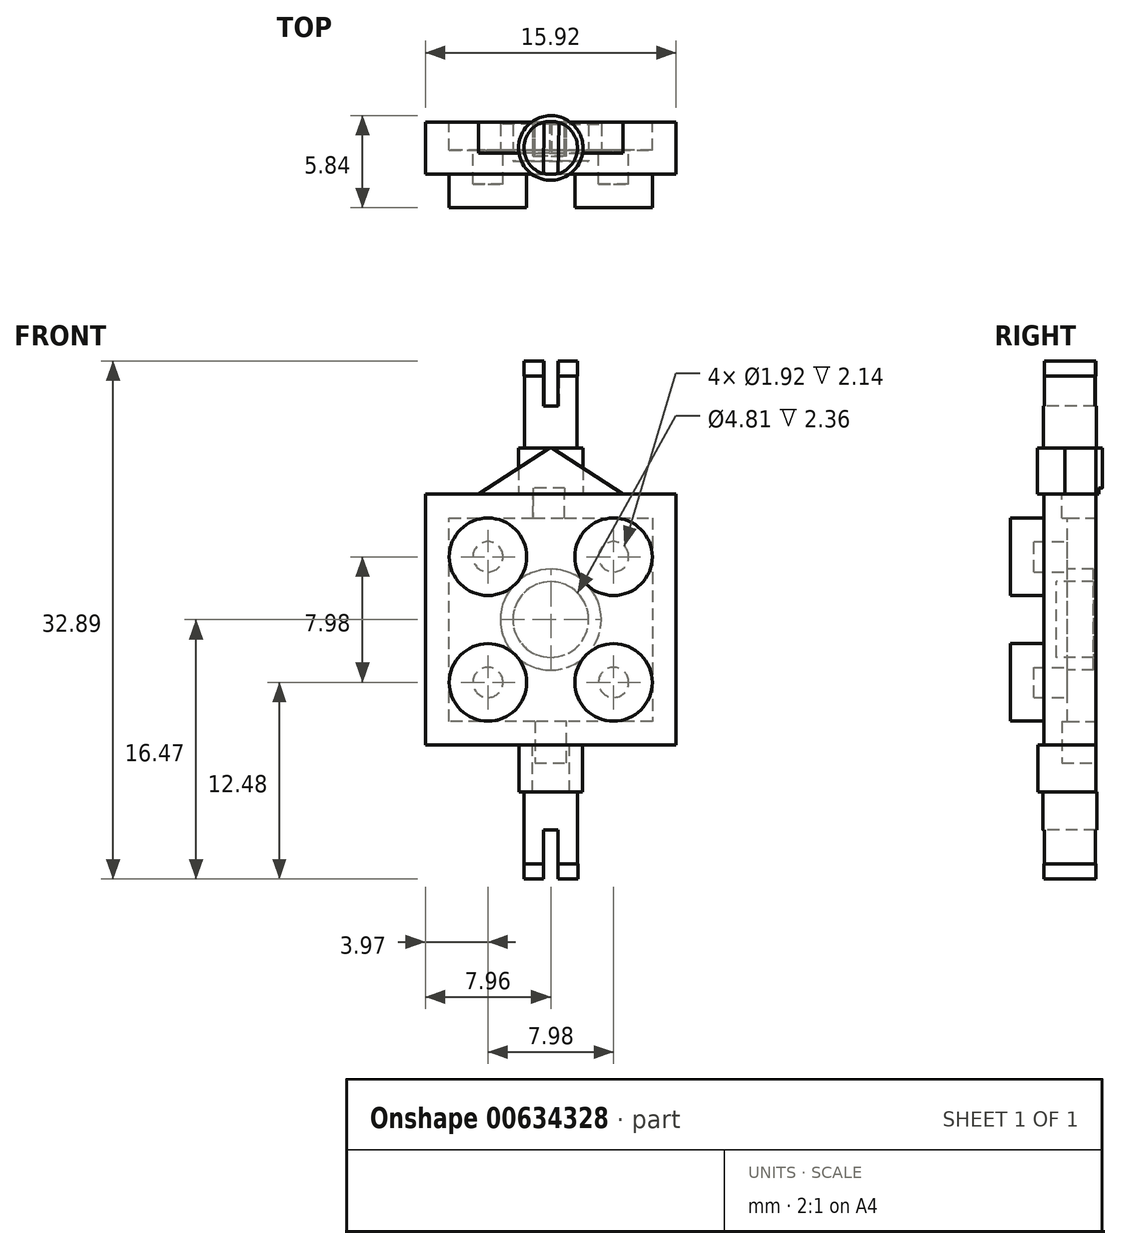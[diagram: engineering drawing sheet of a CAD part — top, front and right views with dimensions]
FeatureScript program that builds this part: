
annotation { "Feature Type Name" : "Feature", "Feature Type Description" : "" }
export const myFeature = defineFeature(function(context is Context, id is Id, definition is map)
    precondition{}
    {
        {
            var Q0;
            Q0=qCreatedBy(makeId("Front.planeOp"),FACE);
            var sketch = newSketch(context, id + "F0", { "sketchPlane" : qUnion([Q0])});
            skLineSegment(sketch, "E0", {"start": v(0, 0) * mm, "end": v(0, 15.92) * mm});
            skLineSegment(sketch, "E1", {"start": v(0, 15.92) * mm, "end": v(15.92, 15.92) * mm});
            skLineSegment(sketch, "E2", {"start": v(15.92, 15.92) * mm, "end": v(15.92, 0) * mm});
            skLineSegment(sketch, "E3", {"start": v(15.92, 0) * mm, "end": v(0, 0) * mm});
            skSolve(sketch);
        }
        {
            var Q0;
            Q0=makeQuery(id+"F0.imprint","IMPRINT",FACE,{"disambiguationData":[TD([[makeQuery(id+"F0.imprint","IMPRINT",EDGE,{"derivedFrom":sQuery(id+"F0.wireOp",EDGE,"E0")}),-1.0]])]});
            extrude(context, id + "F1", {"entities" : qUnion([Q0]), "depth" : 3.3 * mm});
        }
        {
            var Q0;
            Q0=makeQuery(id+"F1.opExtrude","CAP_FACE",FACE,{"disambiguationData":[OSD([sQuery(id+"F0.wireOp",EDGE,"E0"),sQuery(id+"F0.wireOp",EDGE,"E1"),sQuery(id+"F0.wireOp",EDGE,"E2"),sQuery(id+"F0.wireOp",EDGE,"E3")])],"isStart":false});
            var sketch = newSketch(context, id + "F2", { "sketchPlane" : qUnion([Q0])});
            skCircle(sketch, "E4", {"center": v(3.97, 11.95) * mm, "radius": 2.46 * mm});
            skCircle(sketch, "E5", {"center": v(11.95, 11.95) * mm, "radius": 2.46 * mm});
            skCircle(sketch, "E6", {"center": v(3.97, 3.97) * mm, "radius": 2.46 * mm});
            skCircle(sketch, "E7", {"center": v(11.95, 3.97) * mm, "radius": 2.46 * mm});
            skSolve(sketch);
        }
        {
            var Q0;
            Q0=qSketchRegion(id+"F2",true);
            extrude(context, id + "F3", {"entities" : qUnion([Q0]), "operationType" : NewBodyOperationType.ADD, "depth" : 2.14 * mm});
        }
        {
            var Q0;
            Q0=makeQuery(id+"F1.opExtrude","CAP_FACE",FACE,{"disambiguationData":[OSD([sQuery(id+"F0.wireOp",EDGE,"E0"),sQuery(id+"F0.wireOp",EDGE,"E1"),sQuery(id+"F0.wireOp",EDGE,"E2"),sQuery(id+"F0.wireOp",EDGE,"E3")])],"isStart":true});
            shell(context, id + "F4", {"entities" : qUnion([Q0]), "thickness" : 1.5 * mm});
        }
        {
            var Q0;
            Q0=makeQuery(id+"F4.opShell","OFFSET_FACE",FACE,{"disambiguationData":[OSD([sQuery(id+"F0.wireOp",EDGE,"E0"),sQuery(id+"F0.wireOp",EDGE,"E1"),sQuery(id+"F0.wireOp",EDGE,"E2"),sQuery(id+"F0.wireOp",EDGE,"E3")])]});
            var sketch = newSketch(context, id + "F5", { "sketchPlane" : qUnion([Q0])});
            skCircle(sketch, "E8", {"center": v(-7.96, 7.96) * mm, "radius": 3.2 * mm});
            skPoint(sketch, "E8.centerSnap0", {"position": v(-7.96, 14.42) * mm});
            skPoint(sketch, "E8.centerSnap1", {"position": v(-1.5, 7.96) * mm});
            skSolve(sketch);
        }
        {
            var Q0;
            Q0=makeQuery(id+"F5.imprint","IMPRINT",FACE,{"disambiguationData":[TD([[makeQuery(id+"F5.imprint","IMPRINT",EDGE,{"derivedFrom":sQuery(id+"F5.wireOp",EDGE,"E8")}),1.0]])]});
            extrude(context, id + "F6", {"entities" : qUnion([Q0]), "operationType" : NewBodyOperationType.ADD, "depth" : 1.66 * mm});
        }
        {
            var Q0;
            Q0=makeQuery(id+"F6.opExtrude","CAP_FACE",FACE,{"disambiguationData":[OSD([sQuery(id+"F5.wireOp",EDGE,"E8")])],"isStart":false});
            shell(context, id + "F7", {"entities" : qUnion([Q0]), "thickness" : .80 * mm});
        }
        {
            var Q0;
            Q0=makeQuery(id+"F1.opExtrude","SWEPT_FACE",FACE,{"disambiguationData":[OSD([sQuery(id+"F0.wireOp",EDGE,"E3")])]});
            var sketch = newSketch(context, id + "F8", { "sketchPlane" : qUnion([Q0])});
            skCircle(sketch, "E9", {"center": v(7.96, 1.65) * mm, "radius": 2.02 * mm});
            skPoint(sketch, "E9.centerSnap0", {"position": v(7.96, 3.3) * mm});
            skPoint(sketch, "E9.centerSnap1", {"position": v(0, 1.65) * mm});
            skSolve(sketch);
        }
        {
            var Q0;
            {var subQ0=sQuery(id+"F8.wireOp",EDGE,"E9");var subQ1=makeQuery(id+"F1.opExtrude","CAP_EDGE",EDGE,{"disambiguationData":[OSD([sQuery(id+"F0.wireOp",EDGE,"E3")])],"isStart":false});var subQ2=makeQuery(id+"F8.imprint","INTERSECT",VERTEX,{"disambiguationData":[OD(0.0)],"derivedFrom":[subQ1,subQ0]});Q0=makeQuery(id+"F8.imprint","IMPRINT",FACE,{"disambiguationData":[TD([[makeQuery(id+"F8.imprint","IMPRINT",EDGE,{"disambiguationData":[TD([[subQ2,1.0]])],"derivedFrom":subQ0}),1.0]])]});}
            var Q1;
            {var subQ0=sQuery(id+"F8.wireOp",EDGE,"E9");var subQ1=makeQuery(id+"F1.opExtrude","CAP_EDGE",EDGE,{"disambiguationData":[OSD([sQuery(id+"F0.wireOp",EDGE,"E3")])],"isStart":true});var subQ2=makeQuery(id+"F8.imprint","INTERSECT",VERTEX,{"disambiguationData":[OD(0.0)],"derivedFrom":[subQ1,subQ0]});Q1=makeQuery(id+"F8.imprint","IMPRINT",FACE,{"disambiguationData":[TD([[makeQuery(id+"F8.imprint","IMPRINT",EDGE,{"disambiguationData":[TD([[subQ2,-1.0]])],"derivedFrom":subQ0}),1.0]])]});}
            var Q2;
            {var subQ0=sQuery(id+"F8.wireOp",EDGE,"E9");var subQ1=sQuery(id+"F0.wireOp",EDGE,"E3");var subQ2=makeQuery(id+"F1.opExtrude","CAP_EDGE",EDGE,{"disambiguationData":[OSD([subQ1])],"isStart":false});var subQ3=makeQuery(id+"F8.imprint","INTERSECT",VERTEX,{"disambiguationData":[OD(0.0)],"derivedFrom":[subQ2,subQ0]});Q2=makeQuery(id+"F8.imprint","IMPRINT",FACE,{"disambiguationData":[TD([[makeQuery(id+"F8.imprint","IMPRINT",EDGE,{"disambiguationData":[TD([[subQ3,-1.0]])],"derivedFrom":subQ0}),1.0]])]});}
            extrude(context, id + "F9", {"entities" : qUnion([Q0, Q1, Q2]), "operationType" : NewBodyOperationType.ADD, "depth" : 8 * mm});
        }
        {
            var Q0;
            Q0=makeQuery(id+"F1.opExtrude","SWEPT_FACE",FACE,{"disambiguationData":[OSD([sQuery(id+"F0.wireOp",EDGE,"E1")])]});
            var sketch = newSketch(context, id + "F10", { "sketchPlane" : qUnion([Q0])});
            skCircle(sketch, "E10", {"center": v(7.96, -1.65) * mm, "radius": 2.05 * mm});
            skPoint(sketch, "E10.centerSnap0", {"position": v(7.96, -3.3) * mm});
            skPoint(sketch, "E10.centerSnap1", {"position": v(15.92, -1.65) * mm});
            skSolve(sketch);
        }
        {
            var Q0;
            {var subQ0=sQuery(id+"F10.wireOp",EDGE,"E10");var subQ1=makeQuery(id+"F1.opExtrude","CAP_EDGE",EDGE,{"disambiguationData":[OSD([sQuery(id+"F0.wireOp",EDGE,"E1")])],"isStart":true});var subQ2=makeQuery(id+"F10.imprint","INTERSECT",VERTEX,{"disambiguationData":[OD(0.0)],"derivedFrom":[subQ1,subQ0]});Q0=makeQuery(id+"F10.imprint","IMPRINT",FACE,{"disambiguationData":[TD([[makeQuery(id+"F10.imprint","IMPRINT",EDGE,{"disambiguationData":[TD([[subQ2,1.0]])],"derivedFrom":subQ0}),1.0]])]});}
            var Q1;
            {var subQ0=sQuery(id+"F10.wireOp",EDGE,"E10");var subQ1=makeQuery(id+"F1.opExtrude","CAP_EDGE",EDGE,{"disambiguationData":[OSD([sQuery(id+"F0.wireOp",EDGE,"E1")])],"isStart":false});var subQ2=makeQuery(id+"F10.imprint","INTERSECT",VERTEX,{"disambiguationData":[OD(0.0)],"derivedFrom":[subQ1,subQ0]});Q1=makeQuery(id+"F10.imprint","IMPRINT",FACE,{"disambiguationData":[TD([[makeQuery(id+"F10.imprint","IMPRINT",EDGE,{"disambiguationData":[TD([[subQ2,-1.0]])],"derivedFrom":subQ0}),1.0]])]});}
            var Q2;
            {var subQ0=sQuery(id+"F10.wireOp",EDGE,"E10");var subQ1=sQuery(id+"F0.wireOp",EDGE,"E1");var subQ2=makeQuery(id+"F1.opExtrude","CAP_EDGE",EDGE,{"disambiguationData":[OSD([subQ1])],"isStart":true});var subQ3=makeQuery(id+"F10.imprint","INTERSECT",VERTEX,{"disambiguationData":[OD(0.0)],"derivedFrom":[subQ2,subQ0]});Q2=makeQuery(id+"F10.imprint","IMPRINT",FACE,{"disambiguationData":[TD([[makeQuery(id+"F10.imprint","IMPRINT",EDGE,{"disambiguationData":[TD([[subQ3,-1.0]])],"derivedFrom":subQ0}),1.0]])]});}
            extrude(context, id + "F11", {"entities" : qUnion([Q0, Q1, Q2]), "operationType" : NewBodyOperationType.ADD, "depth" : 8 * mm});
        }
        {
            var Q0;
            Q0=makeQuery(id+"F1.opExtrude","CAP_FACE",FACE,{"disambiguationData":[OSD([sQuery(id+"F0.wireOp",EDGE,"E0"),sQuery(id+"F0.wireOp",EDGE,"E1"),sQuery(id+"F0.wireOp",EDGE,"E2"),sQuery(id+"F0.wireOp",EDGE,"E3")])],"isStart":true});
            var sketch = newSketch(context, id + "F12", { "sketchPlane" : qUnion([Q0])});
            skLineSegment(sketch, "E11", {"start": v(-3.4, 0) * mm, "end": v(-7.96, 0) * mm});
            skLineSegment(sketch, "E12", {"start": v(-7.96, 0) * mm, "end": v(-7.96, -3) * mm});
            skLineSegment(sketch, "E13", {"start": v(-7.96, -3) * mm, "end": v(-3.4, 0) * mm});
            skLineSegment(sketch, "E14", {"start": v(-7.96, 0) * mm, "end": v(-12.53, 0) * mm});
            skLineSegment(sketch, "E15", {"start": v(-12.53, 0) * mm, "end": v(-7.96, -3) * mm});
            skSolve(sketch);
        }
        {
            var Q0;
            {var subQ0=sQuery(id+"F12.wireOp",EDGE,"E12");Q0=makeQuery(id+"F12.imprint","IMPRINT",FACE,{"disambiguationData":[TD([[makeQuery(id+"F12.imprint","IMPRINT",EDGE,{"derivedFrom":subQ0}),-1.0]])]});}
            var Q1;
            {var subQ2=sQuery(id+"F12.wireOp",EDGE,"E12");Q1=makeQuery(id+"F12.imprint","IMPRINT",FACE,{"disambiguationData":[TD([[makeQuery(id+"F12.imprint","IMPRINT",EDGE,{"derivedFrom":subQ2}),1.0]])]});}
            var Q2;
            Q2=qSketchRegion(id+"F14",true);
            extrude(context, id + "F13", {"entities" : qUnion([Q0, Q1, Q2]), "oppositeDirection" : true, "depth" : 1.95 * mm});
        }
        {
            var Q0;
            Q0=makeQuery(id+"F1.opExtrude","CAP_FACE",FACE,{"disambiguationData":[OSD([sQuery(id+"F0.wireOp",EDGE,"E0"),sQuery(id+"F0.wireOp",EDGE,"E1"),sQuery(id+"F0.wireOp",EDGE,"E2"),sQuery(id+"F0.wireOp",EDGE,"E3")])],"isStart":true});
            var sketch = newSketch(context, id + "F14", { "sketchPlane" : qUnion([Q0])});
            skLineSegment(sketch, "E16", {"start": v(-12.55, 15.92) * mm, "end": v(-7.96, 18.92) * mm});
            skLineSegment(sketch, "E17", {"start": v(-7.96, 18.92) * mm, "end": v(-7.96, 15.92) * mm});
            skLineSegment(sketch, "E18", {"start": v(-7.96, 15.92) * mm, "end": v(-12.55, 15.92) * mm});
            skLineSegment(sketch, "E19", {"start": v(-7.96, 18.92) * mm, "end": v(-3.37, 15.92) * mm});
            skLineSegment(sketch, "E20", {"start": v(-3.37, 15.92) * mm, "end": v(-7.96, 15.92) * mm});
            skSolve(sketch);
        }
        {
            var Q0;
            {var subQ0=sQuery(id+"F14.wireOp",EDGE,"E17");Q0=makeQuery(id+"F14.imprint","IMPRINT",FACE,{"disambiguationData":[TD([[makeQuery(id+"F14.imprint","IMPRINT",EDGE,{"derivedFrom":subQ0}),1.0]])]});}
            var Q1;
            {var subQ0=sQuery(id+"F14.wireOp",EDGE,"E16");Q1=makeQuery(id+"F14.imprint","IMPRINT",FACE,{"disambiguationData":[TD([[makeQuery(id+"F14.imprint","IMPRINT",EDGE,{"derivedFrom":subQ0}),-1.0]])]});}
            extrude(context, id + "F15", {"entities" : qUnion([Q0, Q1]), "oppositeDirection" : true, "depth" : 1.98 * mm});
        }
        {
            var Q0;
            Q0=makeQuery(id+"F11.opExtrude","CAP_FACE",FACE,{"disambiguationData":[OSD([sQuery(id+"F10.wireOp",EDGE,"E10")])],"isStart":false});
            var sketch = newSketch(context, id + "F16", { "sketchPlane" : qUnion([Q0])});
            skCircle(sketch, "E21", {"center": v(7.96, -1.65) * mm, "radius": 3 * mm});
            skSolve(sketch);
        }
        {
            var Q0;
            Q0=qSketchRegion(id+"F16",true);
            extrude(context, id + "F17", {"entities" : qUnion([Q0]), "operationType" : NewBodyOperationType.REMOVE, "oppositeDirection" : true, "depth" : 5.05 * mm});
        }
        {
            var Q0;
            Q0=makeQuery(id+"F17.boolean.opBoolean","COPY",FACE,{"derivedFrom":makeQuery(id+"F17.opExtrude","CAP_FACE",FACE,{"disambiguationData":[OSD([sQuery(id+"F16.wireOp",EDGE,"E21")])],"isStart":false})});
            var sketch = newSketch(context, id + "F18", { "sketchPlane" : qUnion([Q0])});
            skCircle(sketch, "E22", {"center": v(7.96, -1.65) * mm, "radius": 1.68 * mm});
            skSolve(sketch);
        }
        {
            var Q0;
            Q0=qSketchRegion(id+"F18",true);
            extrude(context, id + "F19", {"entities" : qUnion([Q0]), "depth" : 4.55 * mm});
        }
        {
            var Q0;
            Q0=makeQuery(id+"F19.opExtrude","CAP_FACE",FACE,{"disambiguationData":[OSD([sQuery(id+"F18.wireOp",EDGE,"E22")])],"isStart":false});
            var sketch = newSketch(context, id + "F20", { "sketchPlane" : qUnion([Q0])});
            skCircle(sketch, "E23", {"center": v(7.96, -1.65) * mm, "radius": 1.7 * mm});
            skSolve(sketch);
        }
        {
            var Q0;
            Q0=qSketchRegion(id+"F20",true);
            var Q1;
            Q1=qSketchRegion(id+"F22",true);
            var Q2;
            Q2=qSketchRegion(id+"F24",true);
            extrude(context, id + "F21", {"entities" : qUnion([Q0, Q1, Q2]), "operationType" : NewBodyOperationType.ADD, "depth" : .96 * mm});
        }
        {
            var Q0;
            Q0=makeQuery(id+"F21.opExtrude","CAP_FACE",FACE,{"disambiguationData":[OSD([sQuery(id+"F20.wireOp",EDGE,"E23")])],"isStart":false});
            var sketch = newSketch(context, id + "F22", { "sketchPlane" : qUnion([Q0])});
            skLineSegment(sketch, "E24", {"start": v(8.5, 0.64) * mm, "end": v(7.55, 0.64) * mm});
            skLineSegment(sketch, "E25", {"start": v(8.43, -3.28) * mm, "end": v(8.5, 0.64) * mm});
            skLineSegment(sketch, "E26", {"start": v(7.55, 0.64) * mm, "end": v(7.49, -3.28) * mm});
            skArc(sketch, "E27", {"start": v(7.49, -3.28) * mm, "mid": v(7.96, -3.35) * mm, "end": v(8.43, -3.28) * mm});
            skSolve(sketch);
        }
        {
            var Q0;
            Q0=qSketchRegion(id+"F22",true);
            extrude(context, id + "F23", {"entities" : qUnion([Q0]), "operationType" : NewBodyOperationType.REMOVE, "oppositeDirection" : true, "depth" : 2.86 * mm});
        }
        {
            var Q0;
            Q0=makeQuery(id+"F9.opExtrude","CAP_FACE",FACE,{"disambiguationData":[OSD([sQuery(id+"F8.wireOp",EDGE,"E9")])],"isStart":false});
            var sketch = newSketch(context, id + "F24", { "sketchPlane" : qUnion([Q0])});
            skCircle(sketch, "E28", {"center": v(7.96, 1.65) * mm, "radius": 2.04 * mm});
            skSolve(sketch);
        }
        {
            var Q0;
            Q0=qSketchRegion(id+"F24",true);
            extrude(context, id + "F25", {"entities" : qUnion([Q0]), "operationType" : NewBodyOperationType.REMOVE, "oppositeDirection" : true, "depth" : 5 * mm});
        }
        {
            var Q0;
            Q0=makeQuery(id+"F25.boolean.opBoolean","COPY",FACE,{"derivedFrom":makeQuery(id+"F25.opExtrude","CAP_FACE",FACE,{"disambiguationData":[OSD([sQuery(id+"F24.wireOp",EDGE,"E28")])],"isStart":false})});
            var sketch = newSketch(context, id + "F26", { "sketchPlane" : qUnion([Q0])});
            skCircle(sketch, "E29", {"center": v(7.96, 1.65) * mm, "radius": 1.7 * mm});
            skSolve(sketch);
        }
        {
            var Q0;
            Q0=qSketchRegion(id+"F26",true);
            extrude(context, id + "F27", {"entities" : qUnion([Q0]), "operationType" : NewBodyOperationType.ADD, "depth" : 4.55 * mm});
        }
        {
            var Q0;
            Q0=makeQuery(id+"F27.opExtrude","CAP_FACE",FACE,{"disambiguationData":[OSD([sQuery(id+"F26.wireOp",EDGE,"E29")])],"isStart":false});
            var sketch = newSketch(context, id + "F28", { "sketchPlane" : qUnion([Q0])});
            skCircle(sketch, "E30", {"center": v(7.96, 1.65) * mm, "radius": 1.72 * mm});
            skSolve(sketch);
        }
        {
            var Q0;
            Q0=qSketchRegion(id+"F28",true);
            extrude(context, id + "F29", {"entities" : qUnion([Q0]), "operationType" : NewBodyOperationType.ADD, "depth" : .96 * mm});
        }
        {
            var Q0;
            Q0=makeQuery(id+"F29.opExtrude","CAP_FACE",FACE,{"disambiguationData":[OSD([sQuery(id+"F28.wireOp",EDGE,"E30")])],"isStart":false});
            var sketch = newSketch(context, id + "F30", { "sketchPlane" : qUnion([Q0])});
            skLineSegment(sketch, "E31", {"start": v(8.43, -0.27) * mm, "end": v(8.43, 3.68) * mm});
            skLineSegment(sketch, "E32", {"start": v(8.43, 3.68) * mm, "end": v(7.5, 3.68) * mm});
            skLineSegment(sketch, "E33", {"start": v(7.5, 3.68) * mm, "end": v(7.5, -0.27) * mm});
            skLineSegment(sketch, "E34", {"start": v(7.5, -0.27) * mm, "end": v(8.43, -0.27) * mm});
            skSolve(sketch);
        }
        {
            var Q0;
            Q0=qSketchRegion(id+"F30",true);
            var Q1;
            Q1=qSketchRegion(id+"F32",true);
            extrude(context, id + "F31", {"entities" : qUnion([Q0, Q1]), "operationType" : NewBodyOperationType.REMOVE, "oppositeDirection" : true, "depth" : 3.1 * mm});
        }
        {
            var Q0;
            Q0=makeQuery(id+"F1.opExtrude","CAP_FACE",FACE,{"disambiguationData":[OSD([sQuery(id+"F0.wireOp",EDGE,"E0"),sQuery(id+"F0.wireOp",EDGE,"E1"),sQuery(id+"F0.wireOp",EDGE,"E2"),sQuery(id+"F0.wireOp",EDGE,"E3")])],"isStart":true});
            var sketch = newSketch(context, id + "F32", { "sketchPlane" : qUnion([Q0])});
            skLineSegment(sketch, "E35", {"start": v(-8.83, 14.42) * mm, "end": v(-8.83, 17.06) * mm});
            skLineSegment(sketch, "E36", {"start": v(-8.83, 17.06) * mm, "end": v(-6.83, 17.06) * mm});
            skLineSegment(sketch, "E37", {"start": v(-6.83, 17.06) * mm, "end": v(-6.83, 14.42) * mm});
            skLineSegment(sketch, "E38", {"start": v(-6.83, 14.42) * mm, "end": v(-8.83, 14.42) * mm});
            skSolve(sketch);
        }
        {
            var Q0;
            {var subQ0=sQuery(id+"F32.wireOp",EDGE,"E38");Q0=makeQuery(id+"F32.imprint","IMPRINT",FACE,{"disambiguationData":[TD([[makeQuery(id+"F32.imprint","IMPRINT",EDGE,{"derivedFrom":subQ0}),-1.0]])]});}
            extrude(context, id + "F33", {"entities" : qUnion([Q0]), "operationType" : NewBodyOperationType.REMOVE, "oppositeDirection" : true, "depth" : 2.16 * mm});
        }
        {
            var Q0;
            Q0=makeQuery(id+"F15.opExtrude","CAP_FACE",FACE,{"disambiguationData":[OSD([sQuery(id+"F14.wireOp",EDGE,"E16"),sQuery(id+"F14.wireOp",EDGE,"E18"),sQuery(id+"F14.wireOp",EDGE,"E19"),sQuery(id+"F14.wireOp",EDGE,"E20")])],"isStart":true});
            var sketch = newSketch(context, id + "F34", { "sketchPlane" : qUnion([Q0])});
            skLineSegment(sketch, "E39", {"start": v(-8.84, 15.8) * mm, "end": v(-8.84, 16.31) * mm});
            skLineSegment(sketch, "E40", {"start": v(-8.84, 15.8) * mm, "end": v(-6.82, 15.8) * mm});
            skLineSegment(sketch, "E41", {"start": v(-8.84, 16.31) * mm, "end": v(-6.82, 16.31) * mm});
            skLineSegment(sketch, "E42", {"start": v(-6.82, 16.31) * mm, "end": v(-6.82, 15.8) * mm});
            skSolve(sketch);
        }
        {
            var Q0;
            Q0=qSketchRegion(id+"F34",true);
            extrude(context, id + "F35", {"entities" : qUnion([Q0]), "operationType" : NewBodyOperationType.REMOVE, "depth" : 2.16 * mm});
        }
        {
            var Q0;
            Q0=makeQuery(id+"F1.opExtrude","CAP_FACE",FACE,{"disambiguationData":[OSD([sQuery(id+"F0.wireOp",EDGE,"E0"),sQuery(id+"F0.wireOp",EDGE,"E1"),sQuery(id+"F0.wireOp",EDGE,"E2"),sQuery(id+"F0.wireOp",EDGE,"E3")])],"isStart":true});
            var sketch = newSketch(context, id + "F36", { "sketchPlane" : qUnion([Q0])});
            skLineSegment(sketch, "E43", {"start": v(-6.95, 1.5) * mm, "end": v(-6.95, -1.14) * mm});
            skLineSegment(sketch, "E44", {"start": v(-6.95, -1.14) * mm, "end": v(-8.95, -1.14) * mm});
            skLineSegment(sketch, "E45", {"start": v(-8.95, -1.14) * mm, "end": v(-8.95, 1.5) * mm});
            skLineSegment(sketch, "E46", {"start": v(-8.95, 1.5) * mm, "end": v(-6.95, 1.5) * mm});
            skSolve(sketch);
        }
        {
            var Q0;
            Q0=qSketchRegion(id+"F36",true);
            extrude(context, id + "F37", {"entities" : qUnion([Q0]), "operationType" : NewBodyOperationType.REMOVE, "oppositeDirection" : true, "depth" : 2.16 * mm});
        }
    });
